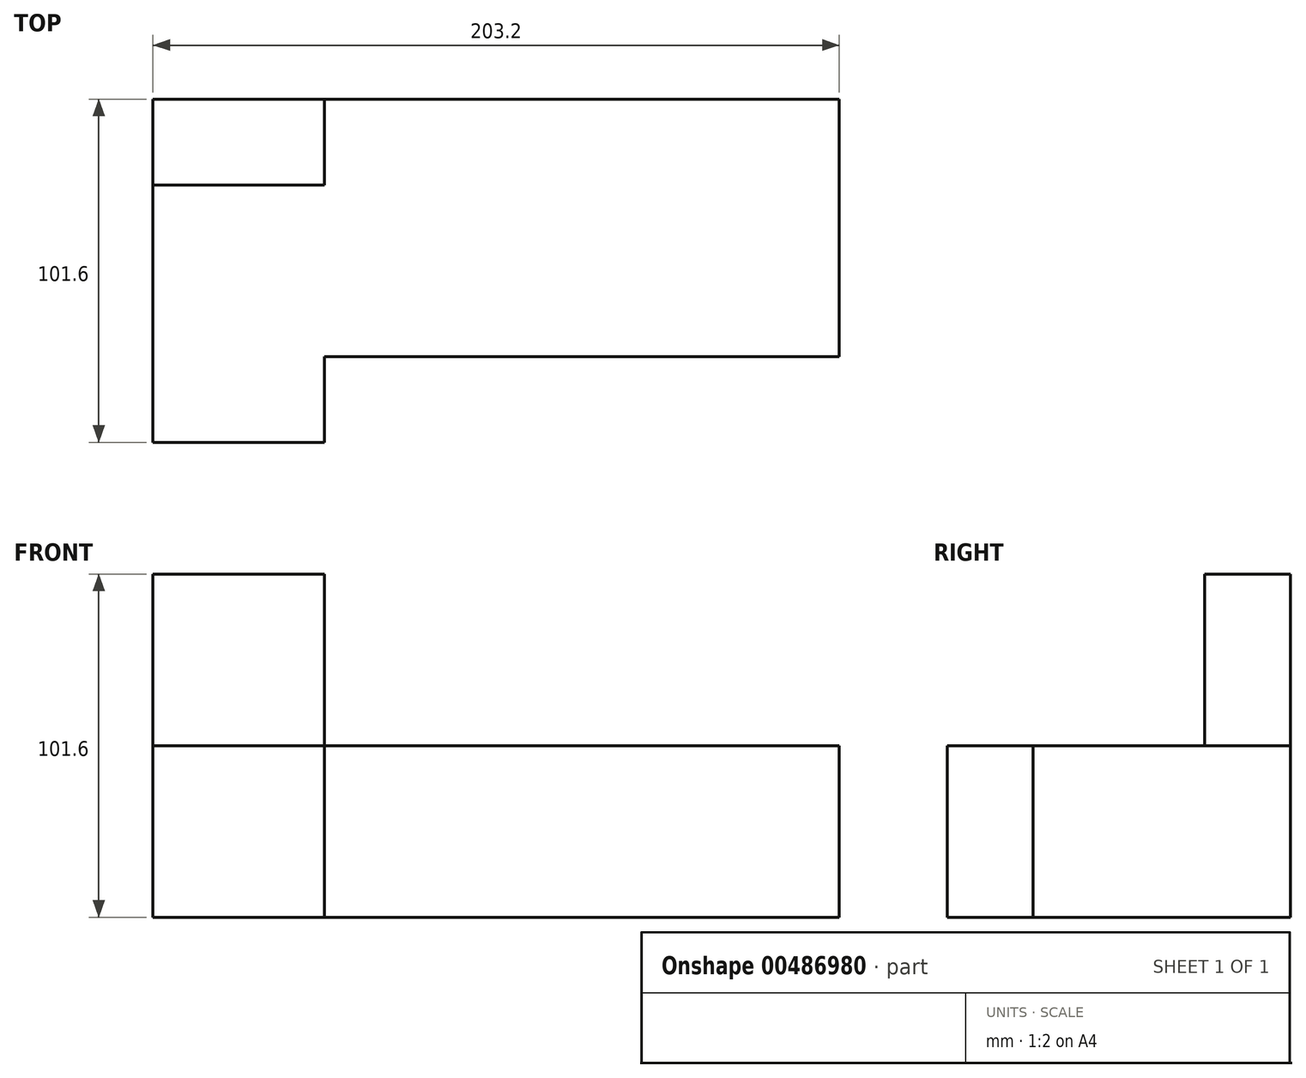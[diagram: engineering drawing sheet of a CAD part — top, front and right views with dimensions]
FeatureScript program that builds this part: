
annotation { "Feature Type Name" : "Feature", "Feature Type Description" : "" }
export const myFeature = defineFeature(function(context is Context, id is Id, definition is map)
    precondition{}
    {
        {
            var Q0;
            Q0=qCreatedBy(makeId("Front.planeOp"),FACE);
            var sketch = newSketch(context, id + "F0", { "sketchPlane" : qUnion([Q0])});
            skLineSegment(sketch, "E0.bottom", {"start": v(-119.56, -35.8) * mm, "end": v(83.64, -35.8) * mm});
            skLineSegment(sketch, "E0.top", {"start": v(-119.56, 15) * mm, "end": v(83.64, 15) * mm});
            skLineSegment(sketch, "E0.left", {"start": v(-119.56, -35.8) * mm, "end": v(-119.56, 15) * mm});
            skLineSegment(sketch, "E0.right", {"start": v(83.64, -35.8) * mm, "end": v(83.64, 15) * mm});
            skSolve(sketch);
        }
        {
            var Q0;
            Q0 = qSketchRegion(id + "F0", true);
            extrude(context, id + "F1", {"entities" : qUnion([Q0]), "depth" : 76.2 * mm});
        }
        {
            var Q0;
            Q0=makeQuery(id+"F1.opExtrude","CAP_FACE",FACE,{"disambiguationData":[OSD([sQuery(id+"F0.wireOp",EDGE,"E0.bottom"),sQuery(id+"F0.wireOp",EDGE,"E0.top"),sQuery(id+"F0.wireOp",EDGE,"E0.left"),sQuery(id+"F0.wireOp",EDGE,"E0.right")])],"isStart":false});
            var sketch = newSketch(context, id + "F2", { "sketchPlane" : qUnion([Q0])});
            skLineSegment(sketch, "E1.bottom", {"start": v(-119.56, -35.8) * mm, "end": v(-68.76, -35.8) * mm});
            skLineSegment(sketch, "E1.top", {"start": v(-119.56, 15) * mm, "end": v(-68.76, 15) * mm});
            skLineSegment(sketch, "E1.left", {"start": v(-119.56, -35.8) * mm, "end": v(-119.56, 15) * mm});
            skLineSegment(sketch, "E1.right", {"start": v(-68.76, -35.8) * mm, "end": v(-68.76, 15) * mm});
            skSolve(sketch);
        }
        {
            var Q0;
            Q0 = qSketchRegion(id + "F2", true);
            extrude(context, id + "F3", {"entities" : qUnion([Q0]), "operationType" : NewBodyOperationType.ADD, "depth" : 25.4 * mm});
        }
        {
            var Q0;
            Q0=qCreatedBy(makeId("Front.planeOp"),FACE);
            var sketch = newSketch(context, id + "F4", { "sketchPlane" : qUnion([Q0])});
            skLineSegment(sketch, "E2.bottom", {"start": v(-119.56, 15) * mm, "end": v(-68.76, 15) * mm});
            skLineSegment(sketch, "E2.top", {"start": v(-119.56, 65.8) * mm, "end": v(-68.76, 65.8) * mm});
            skLineSegment(sketch, "E2.left", {"start": v(-119.56, 15) * mm, "end": v(-119.56, 65.8) * mm});
            skLineSegment(sketch, "E2.right", {"start": v(-68.76, 15) * mm, "end": v(-68.76, 65.8) * mm});
            skSolve(sketch);
        }
        {
            var Q0;
            Q0 = qSketchRegion(id + "F4", true);
            extrude(context, id + "F5", {"entities" : qUnion([Q0]), "operationType" : NewBodyOperationType.ADD, "depth" : 25.4 * mm});
        }
    });
